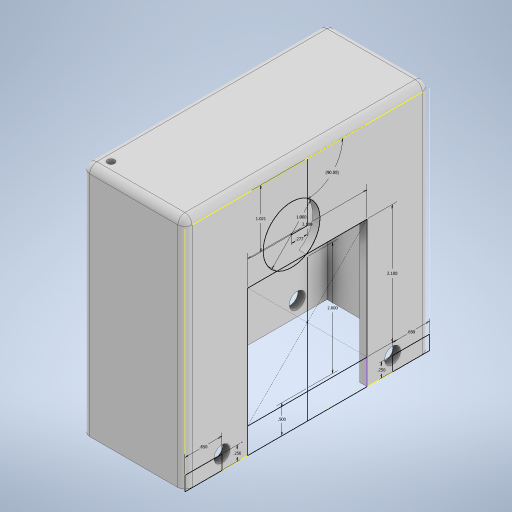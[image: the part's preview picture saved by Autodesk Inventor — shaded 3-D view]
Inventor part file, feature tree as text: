
AUTODESK INVENTOR PART (.ipt)
format: ipt  version: 2024.1 (Build 281209000, 209)  size: 302,080 bytes
history: native  units: in
note: dims shown in document units (in); Inventor stores cm internally (conversion verified against a paired STEP export)
features: extrude x4, sketch x4, hole x2, fillet x1
ambient origin geometry x8: Origin, YZ Plane, XZ Plane, XY Plane, X Axis, Y Axis, Z Axis, Center Point
bodies: Solid1 (feature_tree)
feature tree (11):
  extrude  "Extrusion1"  Depth=4.0in
  sketch  "Sketch2"  dims[d2=0.25in d3=0.25in]
  extrude  "Extrusion2"  Depth=0.25in
  hole  "Hole1"  [1 undecoded]
  extrude  "Extrusion3"  Depth=4.3in
  fillet  "Fillet1"  Radius=4.0in
  extrude  "Extrusion4"  Depth=0.125in
  hole  "Hole2"  [1 undecoded]
  sketch  "Sketch1"  dims[d0=1.0in d1=4.0in]
  sketch  "Sketch3"  dims[d4=1.55in d5=4.05in]
  sketch  "Sketch4"  dims[d6=1.8in d7=4.3in d8=4.0in d9=0.0in d12=0.65in d13=0.25in d14=0.5in d15=2.0in d16=2.1in d17=2.1in d18=0.125in d19=0.0in d20=0.281in d21=0.75in d22=0.438in d23=0.25in d24=0.5635in d25=1.0in d26=0.8108in d27=0.125in d28=0.0in d29=0.125in d30=1.021in d31=90.0deg d33=0.0in d34=0.0in d37=0.277in d38=1.0in d39=0.125in d40=0.125in d41=0.125in d42=0.75in d43=0.375in d44=0.25in d45=0.5635in d46=1.0in d47=0.8108in d48=0.65in d49=0.25in]
note: 2 required parameter values undecoded (feature->parameter linkage not recoverable at this tier; creation-order binding heuristic only, values carry confidence <= 0.55)
